# Revit family: Electronics_Community-Point-Source_Biamp_Loudspeaker_R_5HP
name_source: partatom
category: Communication Devices
units: mm (PartAtom-declared; Revit-internal decimal feet)

## family parameters
Cut with Voids When Loaded = No
Host = Face
Maintain Annotation Orientation = No
OmniClass Number = 23.85.10.11.14.14.14
OmniClass Title = Loudspeakers
Part Type = Normal
Room Calculation Point = No
Round Connector Dimension = Use Diameter
Shared = No

## types (3) — shared parameters
Axial Q / DI = 20.5  / 13.1, 2 kHz to 12.5 kHz
Crossover Frequency = 600 Hz / 4 kHz
Default Elevation = 48 "
Depth = 16.19 "
Description = R.5HP 3-Way Horn Loaded Weather-Resistant Full-Range Loudspeaker
Drivers = LF (1) 12 weather treated, Ferrofluid-cooled MF (1) M200, Ferrofluid-cooled HF (1) 1 exit, titanium free, Ferrofluid-cooled
Enclosure = Rotomolded LLDPE, light grey
Environmental = IEC529 IP55W rating with a minimum 5-degree downward aiming angle
Grill Material = Biamp - Plastic - Gray(Grid)
Grille = 3-layer WeatherStop™, light grey (Zinc-rich epoxy dual-layer powder coated perforated steel grille, foam, woven poly mesh)
Height = 16 "
Housing Material = Biamp - Plastic - Gray
Loudspeaker Type = 3-way, horn loaded coaxial, weather-resistant
Manufacturer = Biamp
Maximum Output = 129 dB SPL / 136 dB SPL (peak)
Minimum Impedance = 3.2 ohms @ 11220 Hz
Mounting/Rigging Provisions = (5) 3/8-16 rigging points
Nominal –6dB Beamwidth = 60° H (+32° / -17°, 2 kHz to 10 kHz); 40° V (+33° / -1°, 2 kHz to 10 kHz)
Product Documentation Link = https://downloads.biamp.com
Product Page URL = https://www.biamp.com
Product data url = https://www.bimobject.com
Recommended Signal Processing = 70 Hz high pass filter
Required Accessories = None
URL = https://www.biamp.com
Width = 16 "
Yoke Material = Biamp - Metal - Gray

## per-type parameters (varying)
| type | 200W Minimum Impedance | 200W Nominal Impedance | Connector Description | Input Connection | Max Input Ratings | Maximum Output on 200W Tap | Nominal Impedance | Operating Range | Recommended Power Amplifier | Sensitivity (1W/1m) | Weight |
| R.5HP |  |  | Terminal strip; 200W continuous, 500W program 35 volts RMS, 77 volts momentary peak | 12 foot (4 m) SJOW #16 gauge | 200W continuous, 500W program 35 volts RMS, 77 volts momentary peak | 125 dB SPL | 6 ohms | 90 Hz to 16 kHz 125 Hz to 12500 Hz (± 6 dB) | 420W to 600W @ 6 ohms | 106 dB SPL (125 Hz to 10 kHz 1/3 octave bands) 107 dB SPL (250 Hz to 4 kHz speech range) | 42.33 lb |
| R.5HPT | 12.1 ohms @ 11 kHz | 25 ohms | Terminal strip; 70V/100V operation | 12 foot (4 m) UV-resistant #18 gauge multi-conductor cable | 200W, 70/100V | 128 dB SPL |  | 90 Hz to 16 kHz 125 Hz to 12500 Hz (± 6 dB) | 25W to 200W @ 70 Volts 50W to 200W @ 100 Volts | 105 dB SPL (125 Hz to 10 kHz 1/3 octave bands) 106 dB SPL (250 Hz to 4 kHz speech range) | 45.42 lb |
| R.5HPT-R | 12.1 ohms @ 11 kHz | 25 ohms | Terminal strip; 70V/100V operation | 12 foot (4 m) UV-resistant #18 gauge multi-conductor cable | 200W, 70/100V | 128 dB SPL |  | 90 Hz to 16 kH 125 Hz to 12500 Hz (± 6 dB) | 25W to 200W @ 70 Volts 50W to 200W @ 100 Volts | 105 dB SPL (125 Hz to 10 kHz 1/3 octave bands) 106 dB SPL (250 Hz to 4 kHz speech range) | 45.42 lb |

note: column(s) folded — value = type name in every type: Model

## geometry (parser evidence)
native form markers: Sweep x4
no freeform markers — native parametric forms only
